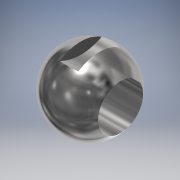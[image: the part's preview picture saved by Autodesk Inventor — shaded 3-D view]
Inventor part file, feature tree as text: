
AUTODESK INVENTOR PART (.ipt)
format: ipt  version: 2018 (Build 220112000, 112)  size: 170,496 bytes
history: native  units: mm (DEFAULTED — no unit token found)
features: sketch x2, extrude x2, revolve x1
ambient origin geometry x8: Origin, YZ Plane, XZ Plane, XY Plane, X Axis, Y Axis, Z Axis, Center Point
bodies: Solid1 (feature_tree)
feature tree (5):
  revolve  "Revolution1"  Angle=90.0deg
  sketch  "Sketch2"  dims[d2=32.0mm d3=10.0mm d4=0.0mm d5=32.0mm d6=50.0mm d7=13.0mm d8=0.0mm]
  extrude  "Extrusion1"  Depth=10.0mm TaperAngle=0.0deg
  extrude  "Extrusion2"  Depth=32.0mm
  sketch  "Sketch1"  dims[d0=54.0mm d1=90.0deg]
